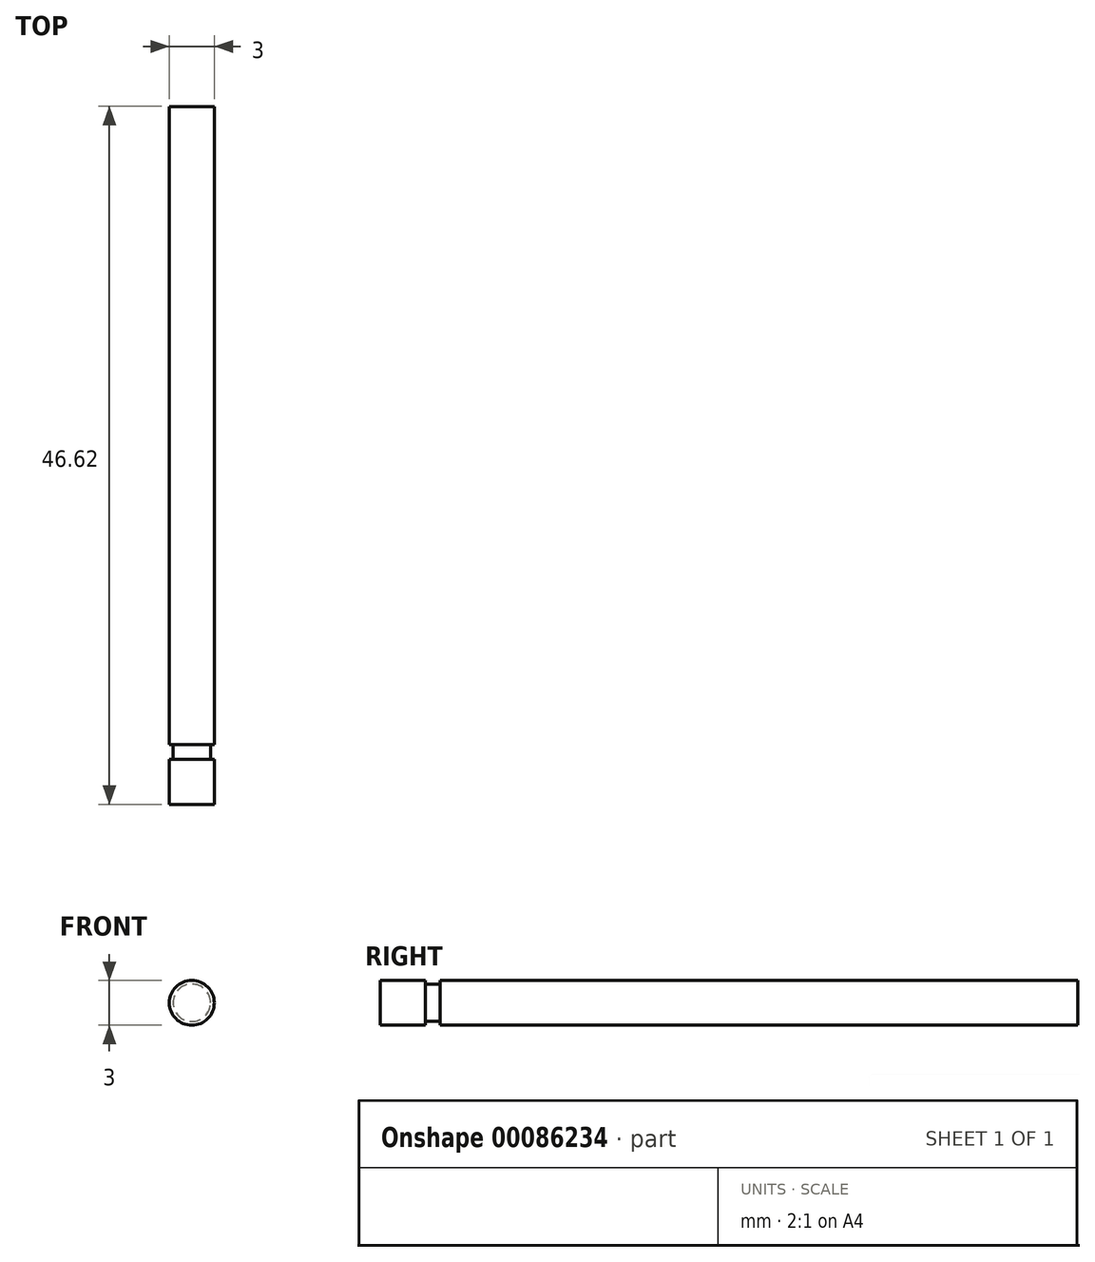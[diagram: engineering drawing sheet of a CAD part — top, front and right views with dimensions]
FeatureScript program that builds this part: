
annotation { "Feature Type Name" : "Feature", "Feature Type Description" : "" }
export const myFeature = defineFeature(function(context is Context, id is Id, definition is map)
    precondition{}
    {
        {
            var Q0;
            Q0=qCreatedBy(makeId("Right.planeOp"),FACE);
            var sketch = newSketch(context, id + "F0", { "sketchPlane" : qUnion([Q0])});
            skLineSegment(sketch, "E0", {"start": v(23.3, 0) * mm, "end": v(23.3, 1.5) * mm});
            skLineSegment(sketch, "E1", {"start": v(23.3, 1.5) * mm, "end": v(-19.3, 1.5) * mm});
            skLineSegment(sketch, "E2", {"start": v(-19.3, 1.5) * mm, "end": v(-19.3, 1.25) * mm});
            skLineSegment(sketch, "E3", {"start": v(-19.3, 1.25) * mm, "end": v(-20.3, 1.25) * mm});
            skLineSegment(sketch, "E4", {"start": v(-20.3, 1.25) * mm, "end": v(-20.3, 1.5) * mm});
            skLineSegment(sketch, "E5", {"start": v(-20.3, 1.5) * mm, "end": v(-23.3, 1.5) * mm});
            skLineSegment(sketch, "E6", {"start": v(-23.3, 1.5) * mm, "end": v(-23.3, 0) * mm});
            skLineSegment(sketch, "E7", {"start": v(-23.3, 0) * mm, "end": v(23.3, 0) * mm});
            skSolve(sketch);
        }
        {
            var Q0;
            Q0 = qSketchRegion(id + "F0", true);
            var Q1;
            Q1=sQuery(id+"F0.wireOp",EDGE,"E7");
            revolve(context, id + "F1", {"entities" : qUnion([Q0]), "axis" : qUnion([Q1]), "revolveType" : RevolveType.FULL});
        }
    });
